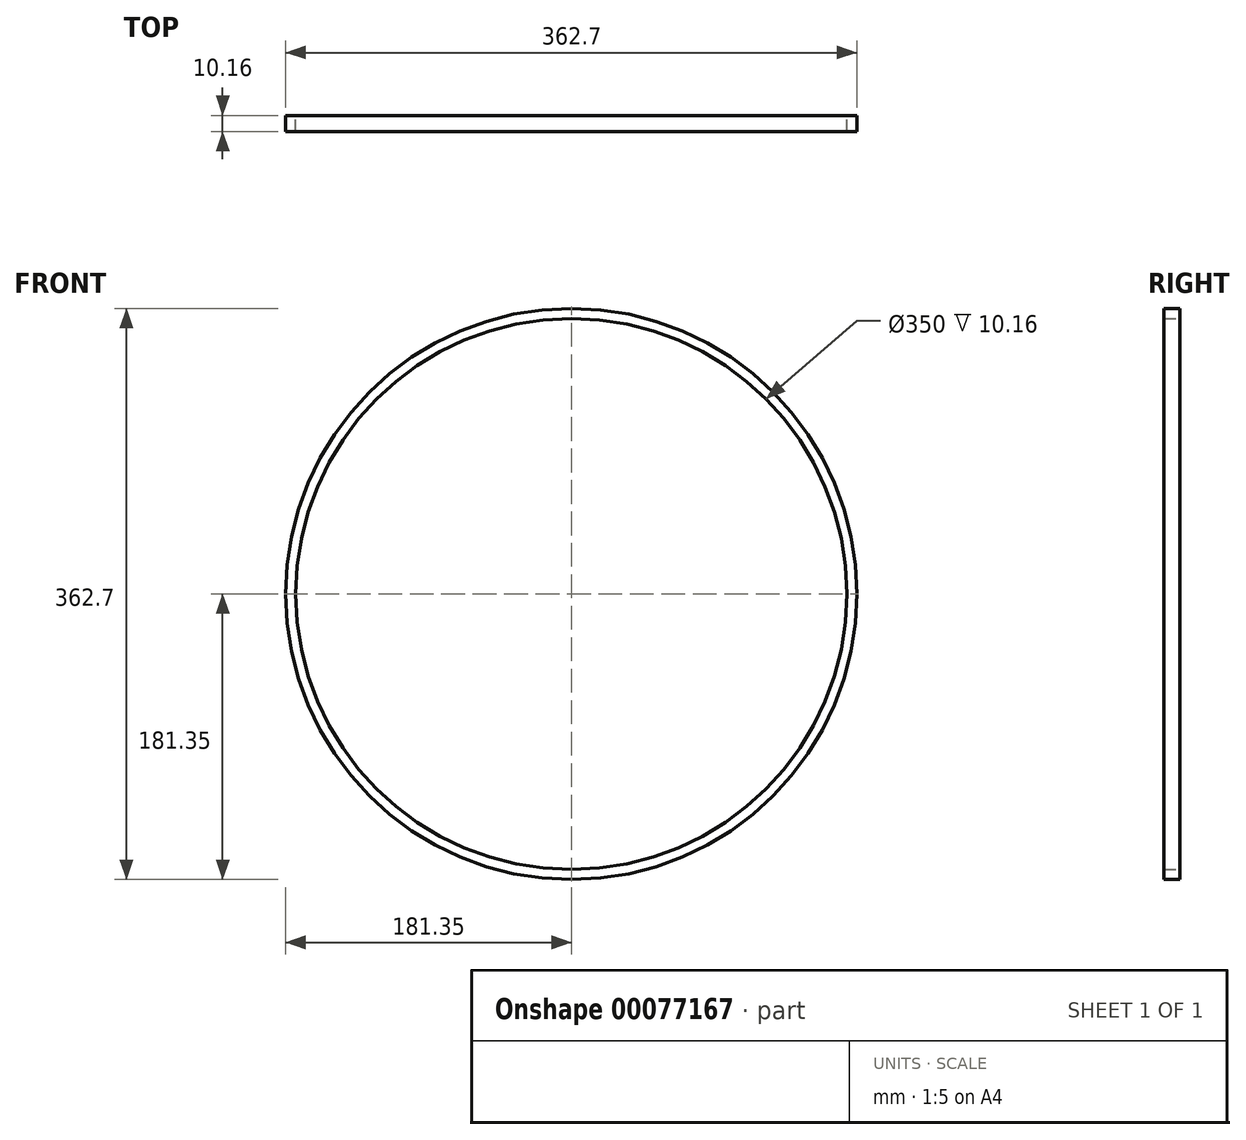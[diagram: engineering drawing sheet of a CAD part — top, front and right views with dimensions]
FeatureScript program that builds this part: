
annotation { "Feature Type Name" : "Feature", "Feature Type Description" : "" }
export const myFeature = defineFeature(function(context is Context, id is Id, definition is map)
    precondition{}
    {
        {
            var Q0;
            Q0=qCreatedBy(makeId("Front.planeOp"),FACE);
            var sketch = newSketch(context, id + "F0", { "sketchPlane" : qUnion([Q0])});
            skCircle(sketch, "E0", {"center": v(0, 0) * mm, "radius": 175 * mm});
            skCircle(sketch, "E1", {"center": v(0, 0) * mm, "radius": 181.35 * mm});
            skSolve(sketch);
        }
        {
            var Q0;
            Q0=makeQuery(id+"F0.imprint","IMPRINT",FACE,{"disambiguationData":[TD([[makeQuery(id+"F0.imprint","IMPRINT",EDGE,{"derivedFrom":sQuery(id+"F0.wireOp",EDGE,"E0")}),-1.0]])]});
            extrude(context, id + "F1", {"entities" : qUnion([Q0]), "depth" : 10.16 * mm});
        }
    });
